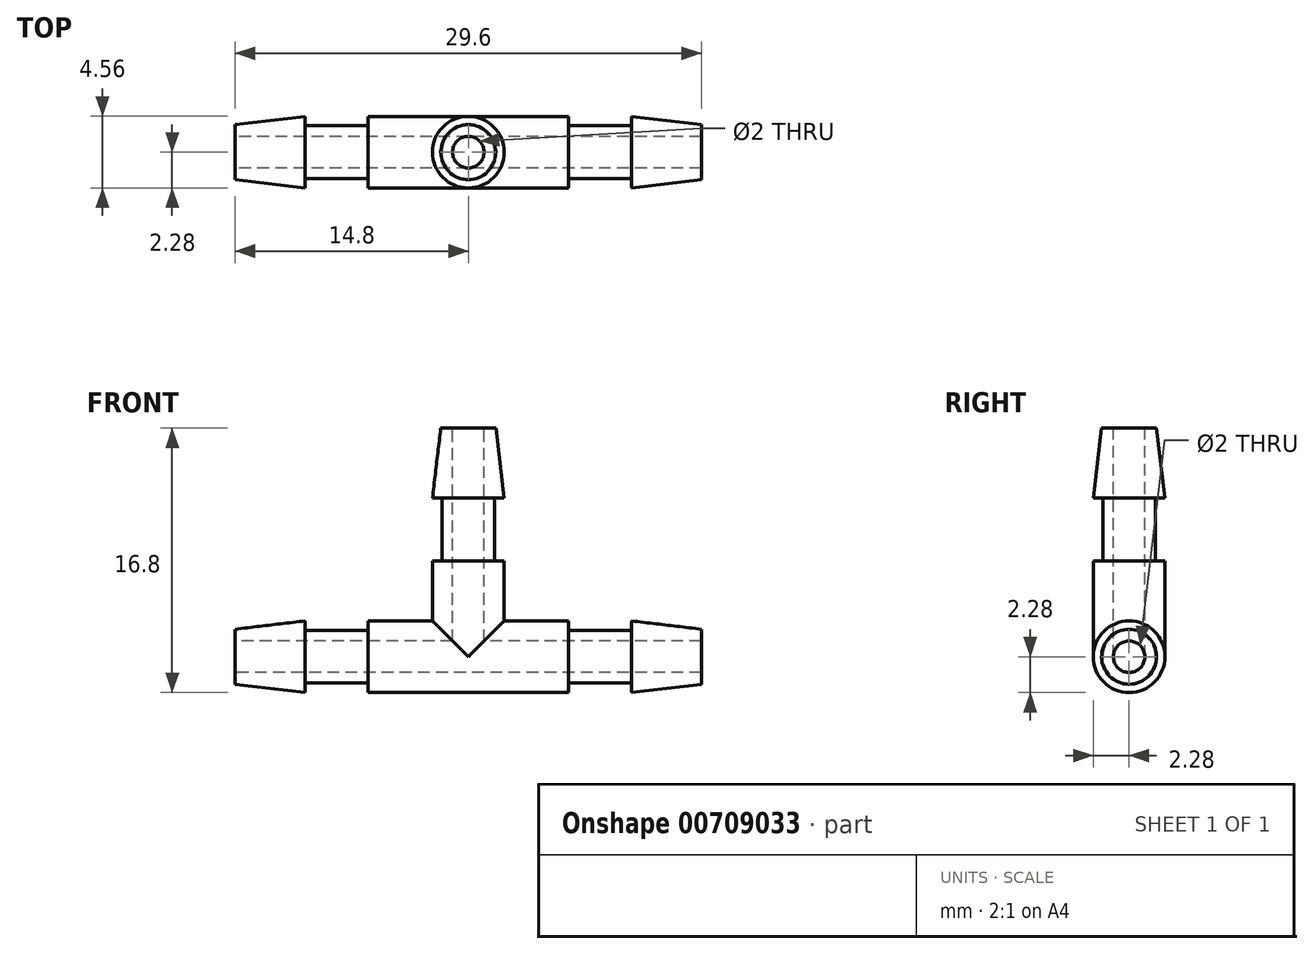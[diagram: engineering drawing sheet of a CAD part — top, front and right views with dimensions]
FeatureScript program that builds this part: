
annotation { "Feature Type Name" : "Feature", "Feature Type Description" : "" }
export const myFeature = defineFeature(function(context is Context, id is Id, definition is map)
    precondition{}
    {
        {
            var Q0;
            Q0=qCreatedBy(makeId("Front.planeOp"),FACE);
            var sketch = newSketch(context, id + "F0", { "sketchPlane" : qUnion([Q0])});
            skLineSegment(sketch, "E0", {"start": v(0, 0) * mm, "end": v(16.75, 0) * mm, "construction": true});
            skLineSegment(sketch, "E1", {"start": v(0, 0) * mm, "end": v(0, 7.84) * mm, "construction": true});
            skLineSegment(sketch, "E2", {"start": v(0, 1) * mm, "end": v(0, 2.27) * mm});
            skLineSegment(sketch, "E3", {"start": v(0, 2.27) * mm, "end": v(6.38, 2.27) * mm});
            skLineSegment(sketch, "E4", {"start": v(6.38, 2.27) * mm, "end": v(6.38, 1.67) * mm});
            skLineSegment(sketch, "E5", {"start": v(6.38, 1.67) * mm, "end": v(10.38, 1.68) * mm});
            skLineSegment(sketch, "E6", {"start": v(10.38, 1.68) * mm, "end": v(10.38, 2.27) * mm});
            skLineSegment(sketch, "E7", {"start": v(10.38, 2.27) * mm, "end": v(14.8, 1.75) * mm});
            skLineSegment(sketch, "E8", {"start": v(14.8, 1.75) * mm, "end": v(14.8, 1) * mm});
            skLineSegment(sketch, "E9.MirrorCS", {"start": v(-10.38, 1.68) * mm, "end": v(-10.38, 2.27) * mm});
            skLineSegment(sketch, "E10.MirrorCS", {"start": v(0, 0) * mm, "end": v(-16.75, 0) * mm, "construction": true});
            skLineSegment(sketch, "E11.MirrorCS", {"start": v(-10.38, 2.27) * mm, "end": v(-14.8, 1.75) * mm});
            skLineSegment(sketch, "E12.MirrorCS", {"start": v(-6.38, 1.67) * mm, "end": v(-10.38, 1.68) * mm});
            skLineSegment(sketch, "E13.MirrorCS", {"start": v(-14.8, 1.75) * mm, "end": v(-14.8, 1) * mm});
            skLineSegment(sketch, "E14.MirrorCS", {"start": v(-6.38, 2.27) * mm, "end": v(-6.38, 1.67) * mm});
            skLineSegment(sketch, "E15.MirrorCS", {"start": v(0, 2.27) * mm, "end": v(-6.38, 2.27) * mm});
            skLineSegment(sketch, "E16", {"start": v(0, 1) * mm, "end": v(14.8, 1) * mm});
            skPoint(sketch, "E17.orphan", {"position": v(14.8, 0) * mm});
            skLineSegment(sketch, "E18.MirrorCS", {"start": v(0, 1) * mm, "end": v(-14.8, 1) * mm});
            skPoint(sketch, "E19.orphan", {"position": v(-14.8, 0) * mm});
            skSolve(sketch);
        }
        {
            var Q0;
            Q0 = qSketchRegion(id + "F0", true);
            var Q1;
            Q1=sQuery(id+"F0.wireOp",EDGE,"E0");
            revolve(context, id + "F1", {"surfaceOperationType" : NewSurfaceOperationType.NEW, "entities" : qUnion([Q0]), "axis" : qUnion([Q1]), "revolveType" : RevolveType.FULL});
        }
        {
            var Q0;
            Q0=qCreatedBy(makeId("Front.planeOp"),FACE);
            var sketch = newSketch(context, id + "F2", { "sketchPlane" : qUnion([Q0])});
            skLineSegment(sketch, "E20", {"start": v(0, 0) * mm, "end": v(0, 17.27) * mm, "construction": true});
            skLineSegment(sketch, "E21", {"start": v(0, 0) * mm, "end": v(4.67, 0) * mm, "construction": true});
            skLineSegment(sketch, "E22", {"start": v(0, 0) * mm, "end": v(0, 14.52) * mm});
            skLineSegment(sketch, "E23", {"start": v(0, 14.52) * mm, "end": v(1.75, 14.52) * mm});
            skLineSegment(sketch, "E24", {"start": v(1.75, 14.52) * mm, "end": v(2.27, 10.1) * mm});
            skLineSegment(sketch, "E25", {"start": v(2.27, 10.1) * mm, "end": v(1.67, 10.1) * mm});
            skLineSegment(sketch, "E26", {"start": v(1.67, 10.1) * mm, "end": v(1.67, 6.1) * mm});
            skLineSegment(sketch, "E27", {"start": v(1.67, 6.1) * mm, "end": v(2.27, 6.1) * mm});
            skLineSegment(sketch, "E28", {"start": v(2.27, 6.1) * mm, "end": v(2.28, 0) * mm});
            skLineSegment(sketch, "E29", {"start": v(2.27, 0) * mm, "end": v(0, 0) * mm});
            skSolve(sketch);
        }
        {
            var Q0;
            Q0 = qSketchRegion(id + "F2", true);
            var Q1;
            Q1=sQuery(id+"F2.wireOp",EDGE,"E20");
            revolve(context, id + "F3", {"operationType" : NewBodyOperationType.ADD, "surfaceOperationType" : NewSurfaceOperationType.NEW, "entities" : qUnion([Q0]), "axis" : qUnion([Q1]), "revolveType" : RevolveType.FULL});
        }
        {
            var Q0;
            Q0=makeQuery(id+"F1.opRevolve","SWEPT_FACE",FACE,{"disambiguationData":[OSD([sQuery(id+"F0.wireOp",EDGE,"E13.MirrorCS")])]});
            var sketch = newSketch(context, id + "F4", { "sketchPlane" : qUnion([Q0])});
            skCircle(sketch, "E30.0", {"center": v(0, 0) * mm, "radius": 1 * mm});
            skSolve(sketch);
        }
        {
            var Q0;
            Q0 = qSketchRegion(id + "F4", true);
            extrude(context, id + "F5", {"entities" : qUnion([Q0]), "operationType" : NewBodyOperationType.REMOVE, "endBound" : BoundingType.THROUGH_ALL, "oppositeDirection" : true, "depth" : 25 * mm, "offsetDistance" : 25 * mm});
        }
        {
            var Q0;
            Q0=makeQuery(id+"F3.opRevolve","SWEPT_FACE",FACE,{"disambiguationData":[OSD([sQuery(id+"F2.wireOp",EDGE,"E23")])]});
            var sketch = newSketch(context, id + "F6", { "sketchPlane" : qUnion([Q0])});
            skCircle(sketch, "E31", {"center": v(0, 0) * mm, "radius": 1 * mm});
            skSolve(sketch);
        }
        {
            var Q0;
            Q0 = qSketchRegion(id + "F6", true);
            var Q1;
            Q1=makeQuery(id+"F5.boolean.opBoolean","MERGE",FACE,{"derivedFrom":[makeQuery(id+"F1.opRevolve","SWEPT_FACE",FACE,{"disambiguationData":[OSD([sQuery(id+"F0.wireOp",EDGE,"E16"),sQuery(id+"F0.wireOp",EDGE,"E18.MirrorCS")])]})],"fromTools":[makeQuery(id+"F5.opExtrude","SWEPT_FACE",FACE,{"disambiguationData":[OSD([sQuery(id+"F4.wireOp",EDGE,"E30.0")])]})]});
            extrude(context, id + "F7", {"entities" : qUnion([Q0]), "operationType" : NewBodyOperationType.REMOVE, "endBound" : BoundingType.UP_TO_SURFACE, "oppositeDirection" : true, "depth" : 25 * mm, "endBoundEntityFace" : qUnion([Q1]), "offsetDistance" : 25 * mm});
        }
    });
